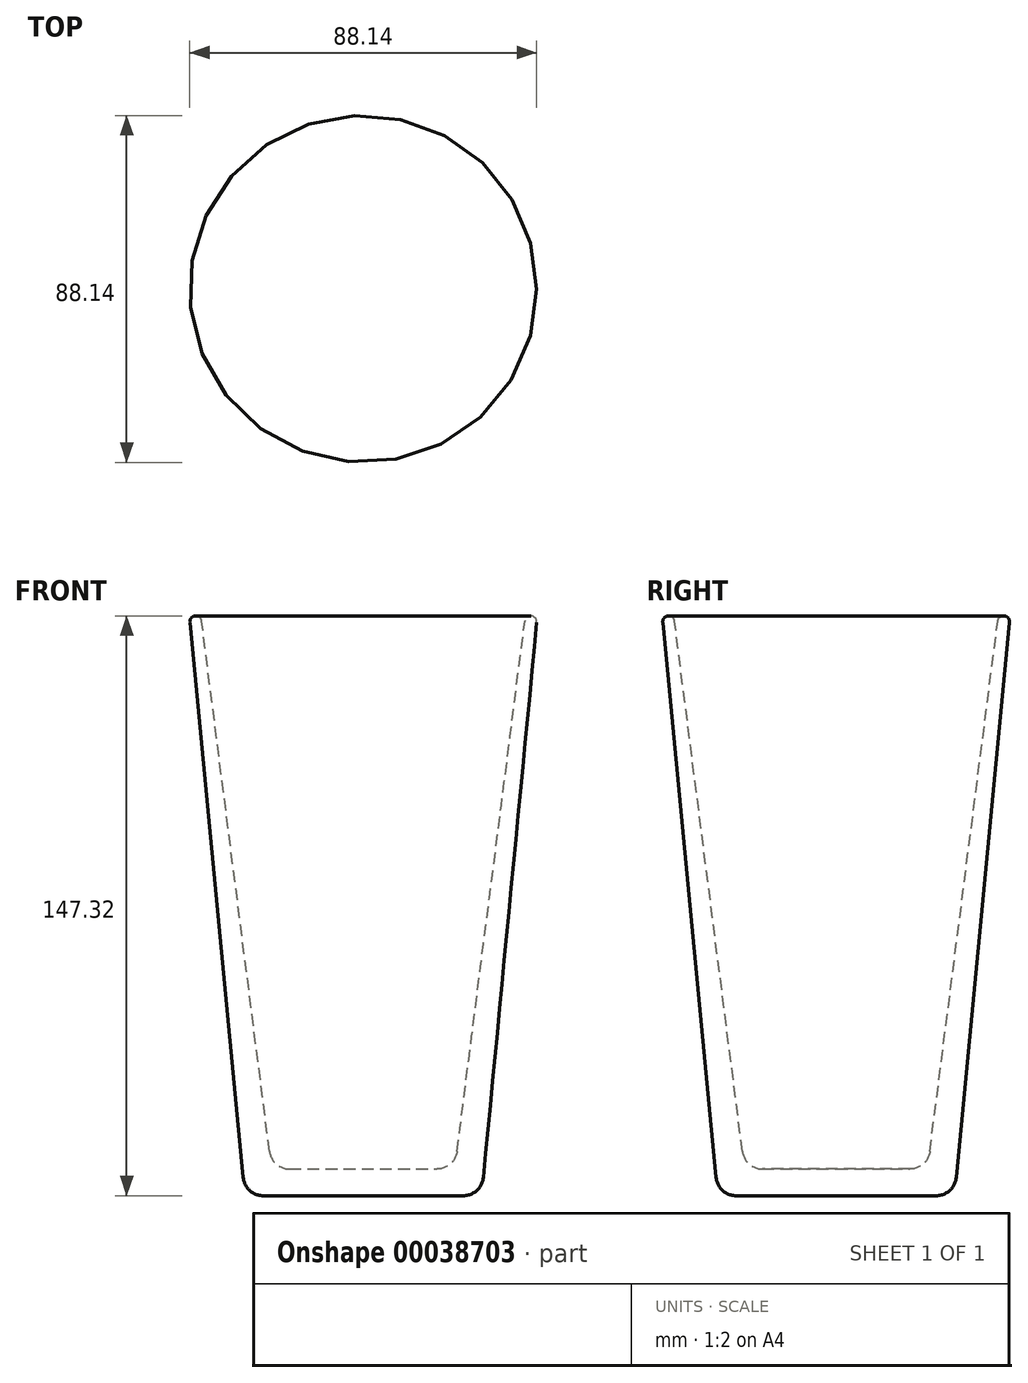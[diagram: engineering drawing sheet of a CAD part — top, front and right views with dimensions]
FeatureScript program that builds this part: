
annotation { "Feature Type Name" : "Feature", "Feature Type Description" : "" }
export const myFeature = defineFeature(function(context is Context, id is Id, definition is map)
    precondition{}
    {
        {
            var Q0;
            Q0=qCreatedBy(makeId("Front.planeOp"),FACE);
            var sketch = newSketch(context, id + "F0", { "sketchPlane" : qUnion([Q0])});
            skLineSegment(sketch, "E0", {"start": v(0, 0) * mm, "end": v(30.06, 0) * mm});
            skLineSegment(sketch, "E1", {"start": v(30.06, 0) * mm, "end": v(44.06, 145.66) * mm});
            skLineSegment(sketch, "E2", {"start": v(41.06, 146) * mm, "end": v(23.24, 6.78) * mm});
            skLineSegment(sketch, "E3", {"start": v(23.24, 6.78) * mm, "end": v(0, 6.78) * mm});
            skLineSegment(sketch, "E4", {"start": v(0, 6.78) * mm, "end": v(0, 0) * mm});
            skArc(sketch, "E5", {"start": v(44.06, 145.66) * mm, "mid": v(42.73, 147.31) * mm, "end": v(41.06, 146) * mm});
            skSolve(sketch);
        }
        {
            var Q0;
            Q0=makeQuery(id+"F0.imprint","IMPRINT",FACE,{"disambiguationData":[TD([[makeQuery(id+"F0.imprint","IMPRINT",EDGE,{"derivedFrom":sQuery(id+"F0.wireOp",EDGE,"E0")}),1.0]])]});
            var Q1;
            Q1=sQuery(id+"F0.wireOp",EDGE,"E4");
            revolve(context, id + "F1", {"entities" : qUnion([Q0]), "axis" : qUnion([Q1]), "revolveType" : RevolveType.FULL});
        }
        {
            var Q0;
            Q0=makeQuery(id+"F1.opRevolve","SWEPT_EDGE",EDGE,{"disambiguationData":[OSD([sQuery(id+"F0.wireOp",EDGE,"E0"),sQuery(id+"F0.wireOp",EDGE,"E1")])]});
            var Q1;
            Q1=makeQuery(id+"F1.opRevolve","SWEPT_EDGE",EDGE,{"disambiguationData":[OSD([sQuery(id+"F0.wireOp",EDGE,"E2"),sQuery(id+"F0.wireOp",EDGE,"E3")])]});
            fillet(context, id + "F2", {"entities" : qUnion([Q0, Q1]), "radius" : 5.08 * mm, "tangentPropagation" : true, "allowEdgeOverflow" : false});
        }
    });
